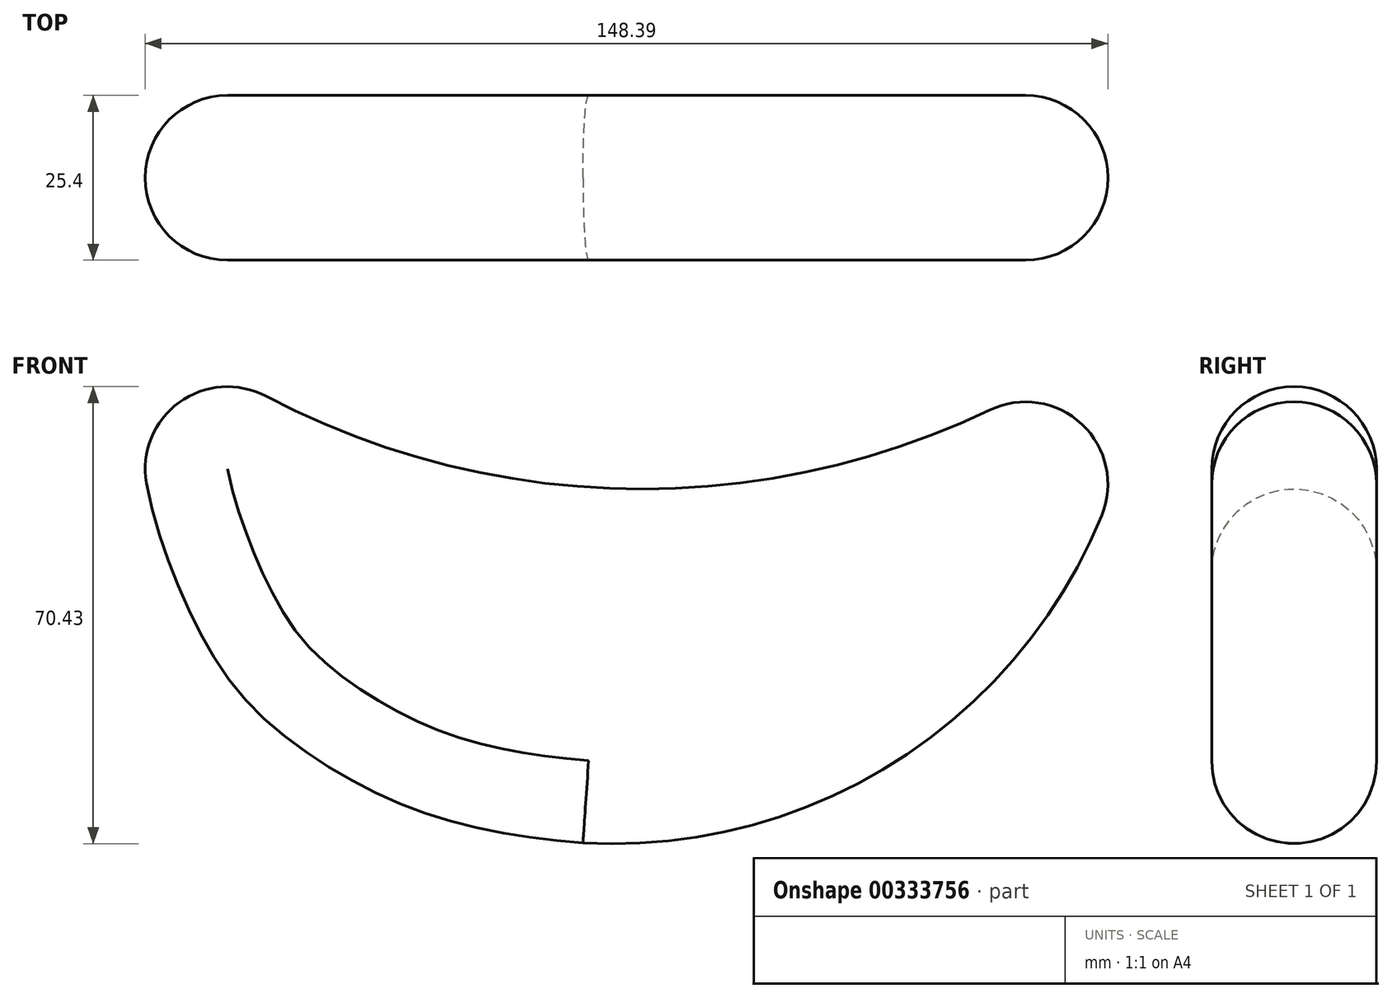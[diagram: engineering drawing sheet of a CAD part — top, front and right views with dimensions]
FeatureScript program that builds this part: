
annotation { "Feature Type Name" : "Feature", "Feature Type Description" : "" }
export const myFeature = defineFeature(function(context is Context, id is Id, definition is map)
    precondition{}
    {
        {
            var Q0;
            Q0=qCreatedBy(makeId("Front.planeOp"),FACE);
            var sketch = newSketch(context, id + "F0", { "sketchPlane" : qUnion([Q0])});
            skPoint(sketch, "E0.middle", {"position": v(0, 0) * mm});
            skArc(sketch, "E1", {"start": v(-76.95, 40.6) * mm, "mid": v(0, 13.94) * mm, "end": v(76.95, 40.6) * mm});
            skFitSpline(sketch, "E2", {"points": [v(-76.95, 40.6) * mm, v(-76.95, 19.87) * mm, v(-74.3, 6.82) * mm, v(-66.37, -11.25) * mm, v(-55.5, -23.78) * mm, v(-34.66, -35.58) * mm, v(-9.04, -40.6) * mm], "startDerivative": vector(-4.01, -130.36) * mm, "endDerivative": vector(139.29, -11.18) * mm});
            skArc(sketch, "E3", {"start": v(-9.04, -40.6) * mm, "mid": v(51.46, -18.54) * mm, "end": v(76.95, 40.6) * mm});
            skSolve(sketch);
        }
        {
            var Q0;
            Q0=makeQuery(id+"F0.imprint","IMPRINT",FACE,{"disambiguationData":[TD([[makeQuery(id+"F0.imprint","IMPRINT",EDGE,{"derivedFrom":sQuery(id+"F0.wireOp",EDGE,"E1")}),-1.0]])]});
            extrude(context, id + "F1", {"entities" : qUnion([Q0]), "depth" : 25.4 * mm});
        }
        {
            var Q0;
            Q0=makeQuery(id+"F1.opExtrude","SWEPT_EDGE",EDGE,{"disambiguationData":[OSD([sQuery(id+"F0.wireOp",EDGE,"E1"),sQuery(id+"F0.wireOp",EDGE,"E2")])]});
            var Q1;
            Q1=makeQuery(id+"F1.opExtrude","SWEPT_EDGE",EDGE,{"disambiguationData":[OSD([sQuery(id+"F0.wireOp",EDGE,"E1"),sQuery(id+"F0.wireOp",EDGE,"E3")])]});
            fillet(context, id + "F2", {"entities" : qUnion([Q0, Q1]), "radius" : 12.7 * mm, "tangentPropagation" : true, "allowEdgeOverflow" : false});
        }
        {
            var Q0;
            Q0=makeQuery(id+"F1.opExtrude","CAP_FACE",FACE,{"disambiguationData":[OSD([sQuery(id+"F0.wireOp",EDGE,"E1"),sQuery(id+"F0.wireOp",EDGE,"E2"),sQuery(id+"F0.wireOp",EDGE,"E3")])],"isStart":false});
            var Q1;
            Q1=makeQuery(id+"F1.opExtrude","CAP_FACE",FACE,{"disambiguationData":[OSD([sQuery(id+"F0.wireOp",EDGE,"E1"),sQuery(id+"F0.wireOp",EDGE,"E2"),sQuery(id+"F0.wireOp",EDGE,"E3")])],"isStart":true});
            fillet(context, id + "F3", {"entities" : qUnion([Q0, Q1]), "radius" : 12.7 * mm, "tangentPropagation" : true, "allowEdgeOverflow" : false});
        }
    });
